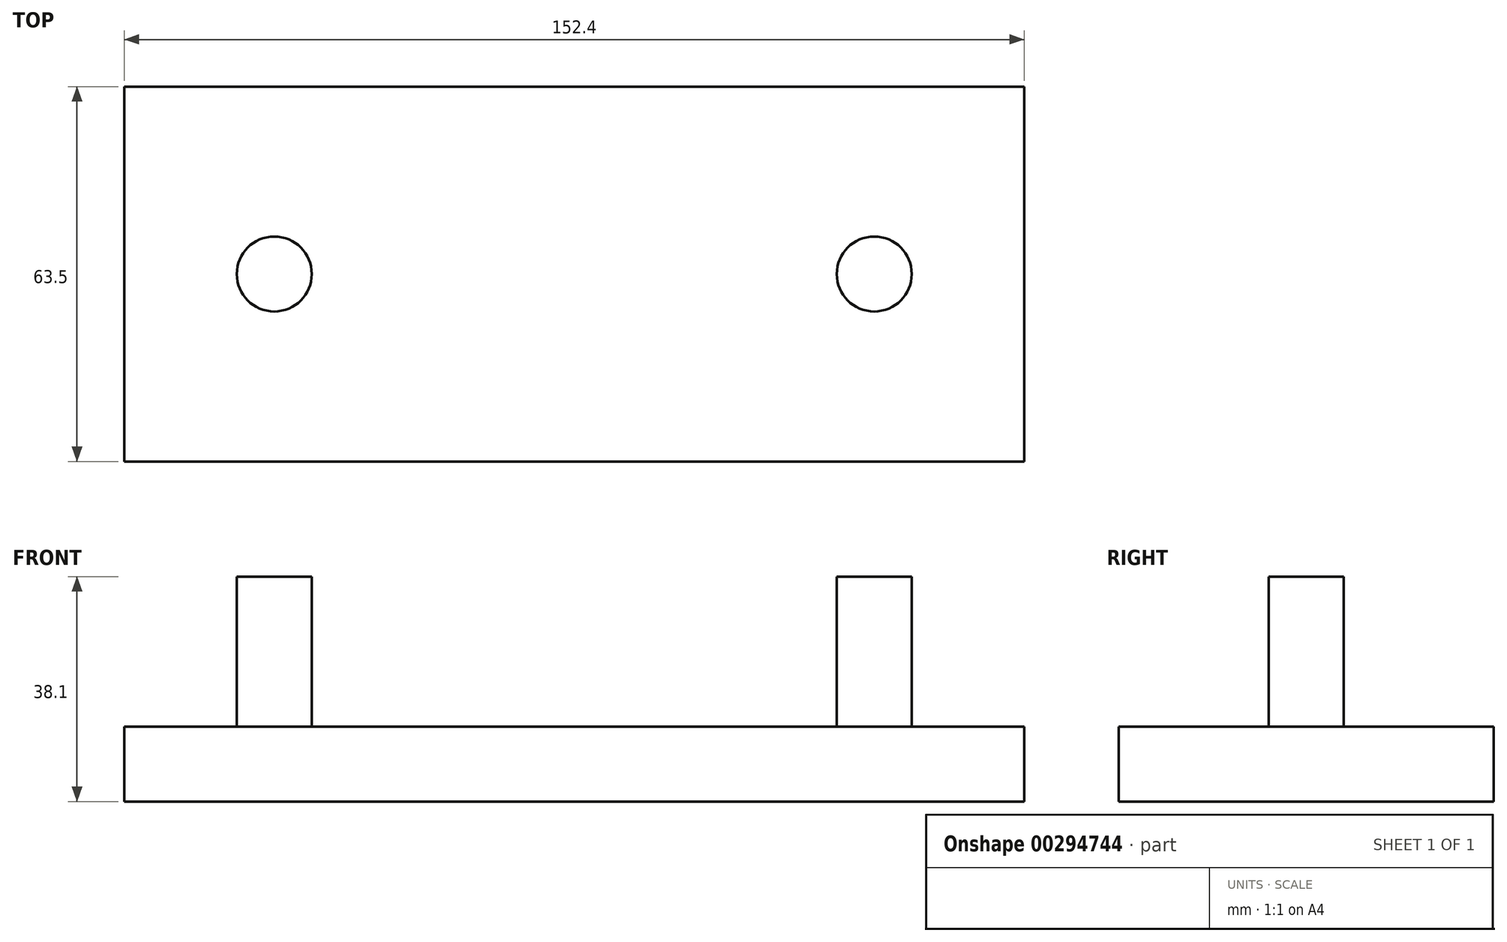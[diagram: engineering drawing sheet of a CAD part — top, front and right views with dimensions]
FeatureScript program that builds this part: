
annotation { "Feature Type Name" : "Feature", "Feature Type Description" : "" }
export const myFeature = defineFeature(function(context is Context, id is Id, definition is map)
    precondition{}
    {
        {
            var Q0;
            Q0=qCreatedBy(makeId("Top.planeOp"),FACE);
            var sketch = newSketch(context, id + "F0", { "sketchPlane" : qUnion([Q0])});
            skLineSegment(sketch, "E0.bottom", {"start": v(-152.4, 31.75) * mm, "end": v(0, 31.75) * mm});
            skLineSegment(sketch, "E0.top", {"start": v(-152.4, -31.75) * mm, "end": v(0, -31.75) * mm});
            skLineSegment(sketch, "E0.left", {"start": v(-152.4, 31.75) * mm, "end": v(-152.4, -31.75) * mm});
            skLineSegment(sketch, "E0.right", {"start": v(0, 31.75) * mm, "end": v(0, -31.75) * mm});
            skCircle(sketch, "E1", {"center": v(-127, 0) * mm, "radius": 6.35 * mm});
            skCircle(sketch, "E2", {"center": v(-25.4, 0) * mm, "radius": 6.35 * mm});
            skSolve(sketch);
        }
        {
            var Q0;
            Q0 = qSketchRegion(id + "F0", true);
            extrude(context, id + "F1", {"entities" : qUnion([Q0]), "depth" : 12.7 * mm});
        }
        {
            var Q0;
            Q0=makeQuery(id+"F0.imprint","IMPRINT",FACE,{"disambiguationData":[TD([[makeQuery(id+"F0.imprint","IMPRINT",EDGE,{"derivedFrom":sQuery(id+"F0.wireOp",EDGE,"E1")}),1.0]])]});
            var Q1;
            Q1=makeQuery(id+"F0.imprint","IMPRINT",FACE,{"disambiguationData":[TD([[makeQuery(id+"F0.imprint","IMPRINT",EDGE,{"derivedFrom":sQuery(id+"F0.wireOp",EDGE,"E2")}),1.0]])]});
            extrude(context, id + "F2", {"entities" : qUnion([Q0, Q1]), "operationType" : NewBodyOperationType.ADD, "depth" : 38.1 * mm});
        }
    });
